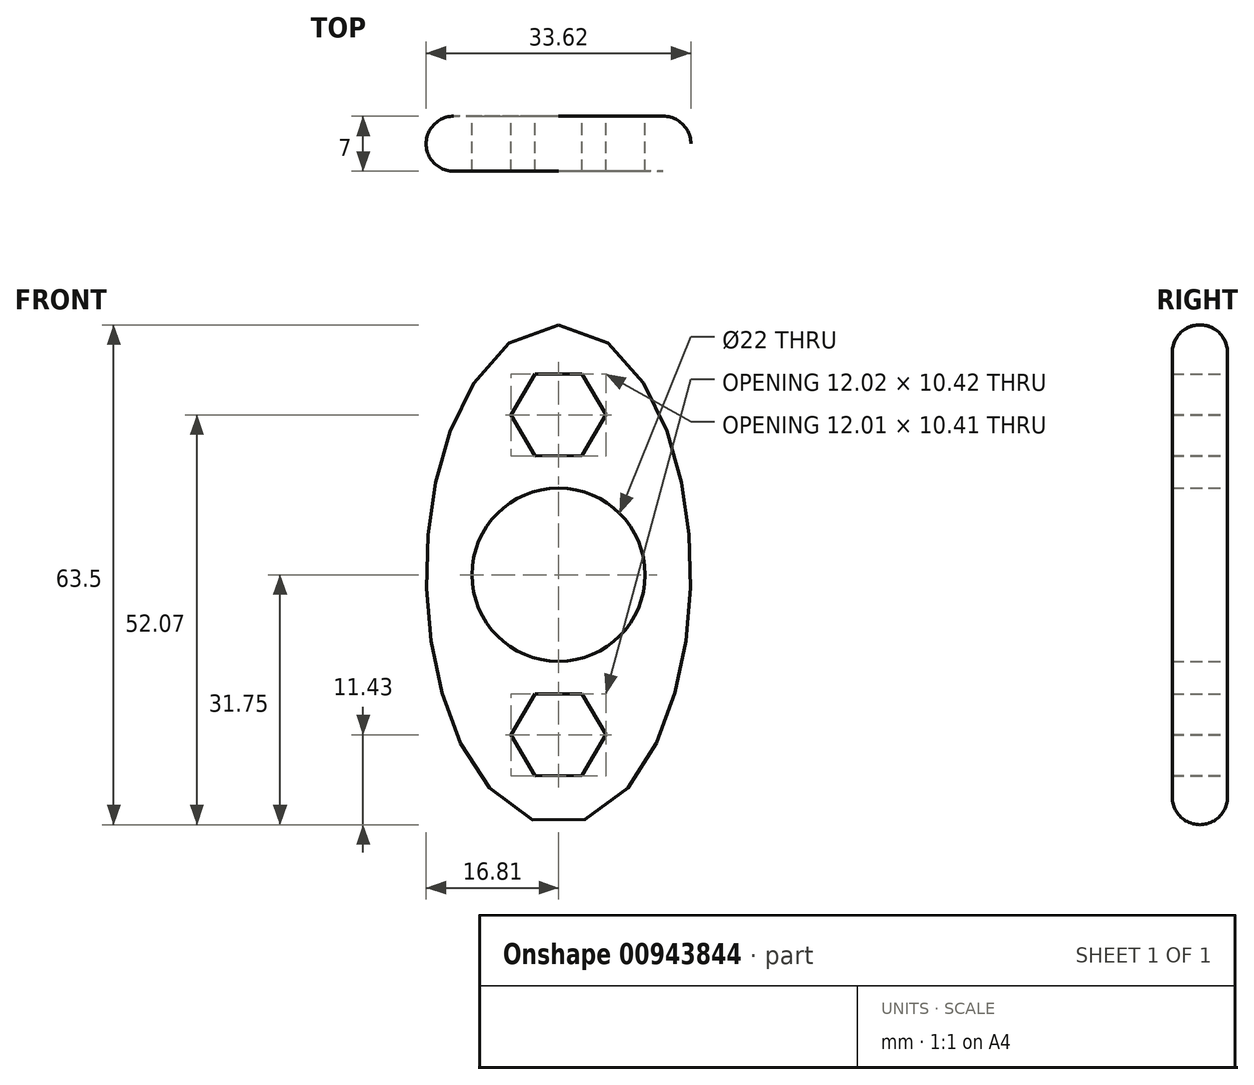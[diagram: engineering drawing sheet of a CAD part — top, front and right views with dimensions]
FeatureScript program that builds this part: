
annotation { "Feature Type Name" : "Feature", "Feature Type Description" : "" }
export const myFeature = defineFeature(function(context is Context, id is Id, definition is map)
    precondition{}
    {
        {
            var Q0;
            Q0=qCreatedBy(makeId("Front.planeOp"),FACE);
            var sketch = newSketch(context, id + "F0", { "sketchPlane" : qUnion([Q0])});
            skEllipse(sketch, "E0", {"center": v(0, 0) * mm, "majorRadius": 31.75 * mm, "minorRadius": 16.81 * mm, "majorAxis": v(0, 1)});
            skCircle(sketch, "E1", {"center": v(0, 0) * mm, "radius": 11 * mm});
            skCircle(sketch, "E2.cCircle", {"center": v(0, 20.32) * mm, "radius": 5.2 * mm, "construction": true});
            skPoint(sketch, "E2.cCircle.centerSnap0", {"position": v(0, 31.75) * mm});
            skLineSegment(sketch, "E2.0", {"start": v(6, 20.33) * mm, "end": v(3, 15.12) * mm});
            skLineSegment(sketch, "E2.1", {"start": v(3, 15.12) * mm, "end": v(-3, 15.12) * mm});
            skLineSegment(sketch, "E2.2", {"start": v(-3, 15.12) * mm, "end": v(-6, 20.31) * mm});
            skLineSegment(sketch, "E2.3", {"start": v(-6, 20.31) * mm, "end": v(-3, 25.52) * mm});
            skLineSegment(sketch, "E2.4", {"start": v(-3, 25.52) * mm, "end": v(3, 25.52) * mm});
            skLineSegment(sketch, "E2.5", {"start": v(3, 25.52) * mm, "end": v(6, 20.33) * mm});
            skPoint(sketch, "E2.0.midPoint", {"position": v(4.5, 17.73) * mm});
            skCircle(sketch, "E3.cCircle", {"center": v(0, -20.32) * mm, "radius": 5.2 * mm, "construction": true});
            skLineSegment(sketch, "E3.0", {"start": v(6.01, -20.31) * mm, "end": v(3.01, -25.52) * mm});
            skLineSegment(sketch, "E3.1", {"start": v(3.01, -25.52) * mm, "end": v(-3, -25.53) * mm});
            skLineSegment(sketch, "E3.2", {"start": v(-3, -25.53) * mm, "end": v(-6.01, -20.33) * mm});
            skLineSegment(sketch, "E3.3", {"start": v(-6.01, -20.33) * mm, "end": v(-3.01, -15.12) * mm});
            skLineSegment(sketch, "E3.4", {"start": v(-3.01, -15.12) * mm, "end": v(3, -15.11) * mm});
            skLineSegment(sketch, "E3.5", {"start": v(3, -15.11) * mm, "end": v(6.01, -20.31) * mm});
            skPoint(sketch, "E3.0.midPoint", {"position": v(4.51, -22.92) * mm});
            skSolve(sketch);
        }
        {
            var Q0;
            Q0 = qSketchRegion(id + "F0", true);
            extrude(context, id + "F1", {"entities" : qUnion([Q0]), "depth" : 7 * mm, "offsetDistance" : 25.4 * mm});
        }
        {
            var Q0;
            Q0=makeQuery(id+"F1.opExtrude","CAP_EDGE",EDGE,{"disambiguationData":[OSD([sQuery(id+"F0.wireOp",EDGE,"E0")])],"isStart":false});
            var Q1;
            Q1=makeQuery(id+"F1.opExtrude","CAP_EDGE",EDGE,{"disambiguationData":[OSD([sQuery(id+"F0.wireOp",EDGE,"E0")])],"isStart":true});
            fillet(context, id + "F2", {"entities" : qUnion([Q0, Q1]), "radius" : 3.5 * mm, "tangentPropagation" : true, "allowEdgeOverflow" : false});
        }
    });
